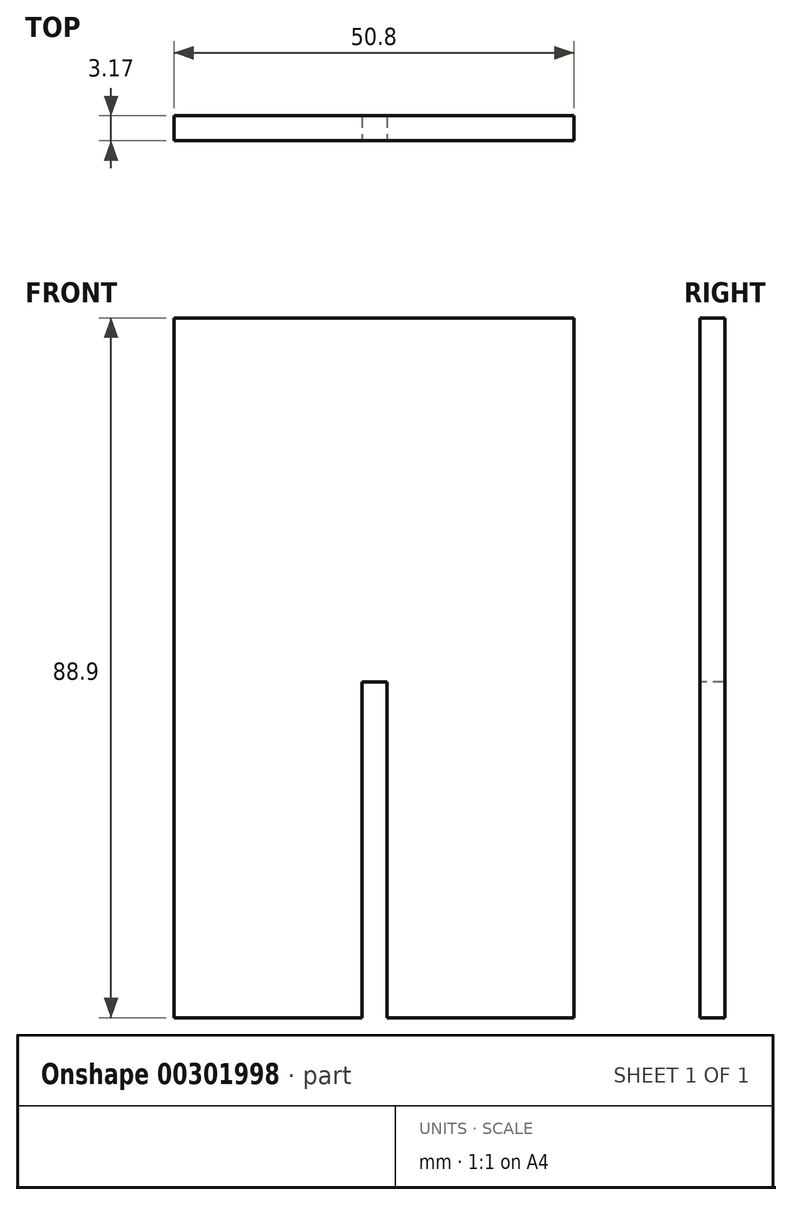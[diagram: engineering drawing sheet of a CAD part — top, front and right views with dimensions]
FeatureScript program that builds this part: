
annotation { "Feature Type Name" : "Feature", "Feature Type Description" : "" }
export const myFeature = defineFeature(function(context is Context, id is Id, definition is map)
    precondition{}
    {
        {
            var Q0;
            Q0=qCreatedBy(makeId("Front.planeOp"),FACE);
            var sketch = newSketch(context, id + "F0", { "sketchPlane" : qUnion([Q0])});
            skLineSegment(sketch, "E0.bottom", {"start": v(-25.4, 44.45) * mm, "end": v(25.4, 44.45) * mm});
            skLineSegment(sketch, "E0.top", {"start": v(-25.4, -44.45) * mm, "end": v(25.4, -44.45) * mm});
            skLineSegment(sketch, "E0.left", {"start": v(-25.4, 44.45) * mm, "end": v(-25.4, -44.45) * mm});
            skLineSegment(sketch, "E0.right", {"start": v(25.4, 44.45) * mm, "end": v(25.4, -44.45) * mm});
            skPoint(sketch, "E0.middle", {"position": v(0, 0) * mm});
            skSolve(sketch);
        }
        {
            var Q0;
            Q0=qSketchRegion(id+"F0",true);
            extrude(context, id + "F1", {"entities" : qUnion([Q0]), "depth" : 3.17 * mm});
        }
        {
            var Q0;
            Q0=makeQuery(id+"F1.opExtrude","CAP_FACE",FACE,{"disambiguationData":[OSD([sQuery(id+"F0.wireOp",EDGE,"E0.bottom"),sQuery(id+"F0.wireOp",EDGE,"E0.top"),sQuery(id+"F0.wireOp",EDGE,"E0.left"),sQuery(id+"F0.wireOp",EDGE,"E0.right")])],"isStart":false});
            var sketch = newSketch(context, id + "F2", { "sketchPlane" : qUnion([Q0])});
            skLineSegment(sketch, "E1", {"start": v(-1.5, -44.45) * mm, "end": v(-1.5, -1.78) * mm});
            skLineSegment(sketch, "E2", {"start": v(1.67, -44.45) * mm, "end": v(1.67, -1.78) * mm});
            skLineSegment(sketch, "E3", {"start": v(-1.5, -44.45) * mm, "end": v(1.67, -44.45) * mm});
            skLineSegment(sketch, "E4", {"start": v(-1.5, -1.78) * mm, "end": v(1.67, -1.78) * mm});
            skSolve(sketch);
        }
        {
            var Q0;
            Q0=makeQuery(id+"F2.imprint","IMPRINT",FACE,{"disambiguationData":[TD([[makeQuery(id+"F2.imprint","IMPRINT",EDGE,{"derivedFrom":sQuery(id+"F2.wireOp",EDGE,"E1")}),-1.0]])]});
            extrude(context, id + "F3", {"entities" : qUnion([Q0]), "operationType" : NewBodyOperationType.REMOVE, "endBound" : BoundingType.THROUGH_ALL, "oppositeDirection" : true, "depth" : 25.4 * mm});
        }
    });
